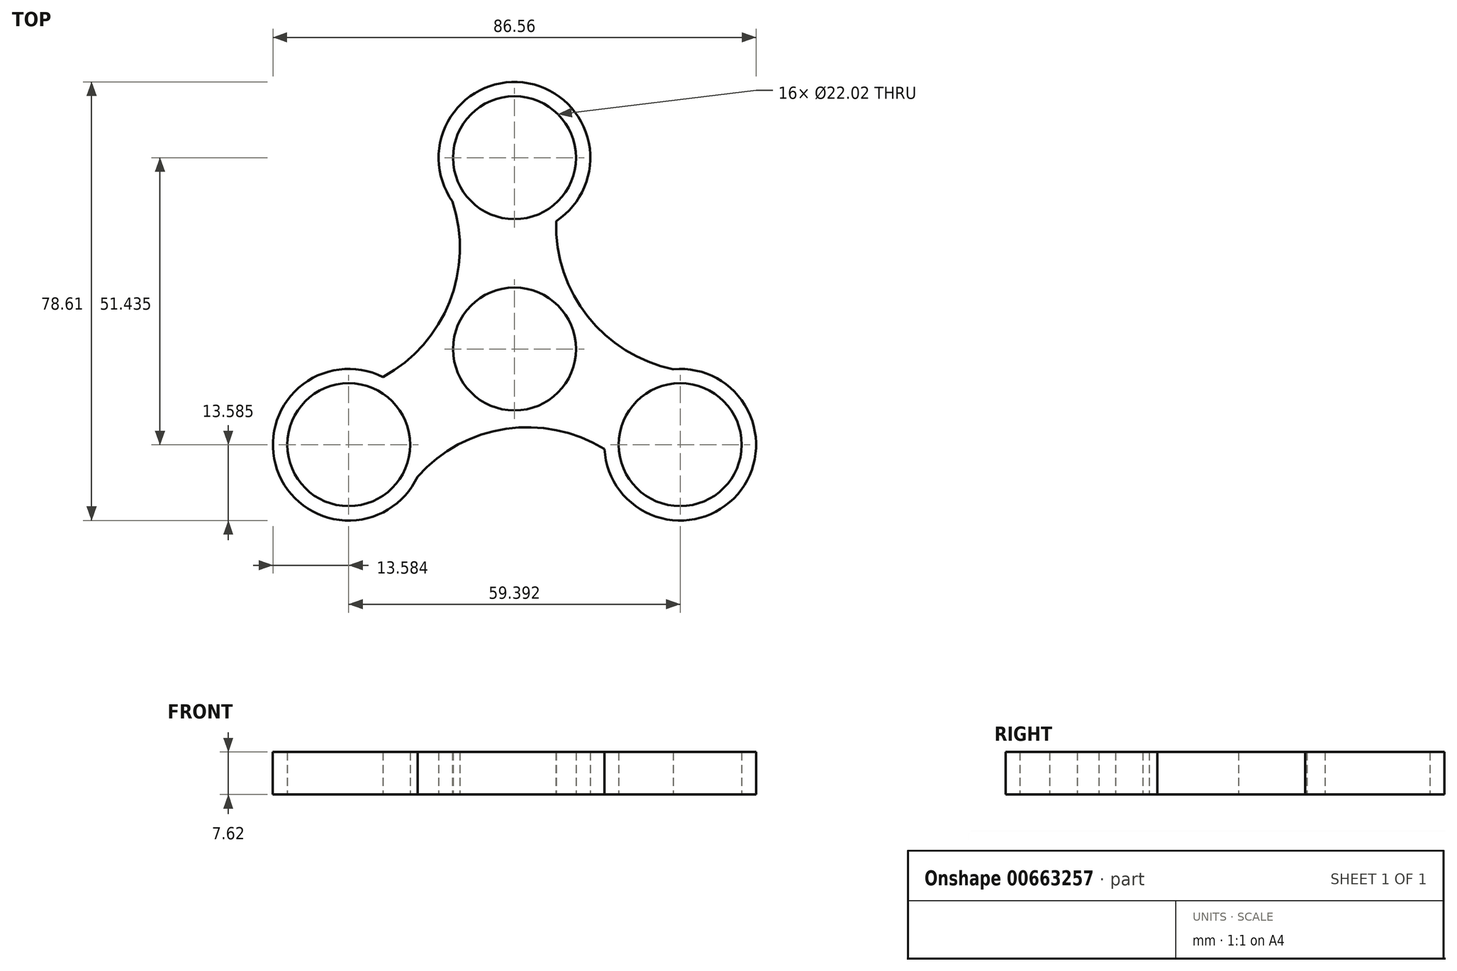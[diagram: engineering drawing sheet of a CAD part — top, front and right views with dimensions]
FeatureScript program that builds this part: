
annotation { "Feature Type Name" : "Feature", "Feature Type Description" : "" }
export const myFeature = defineFeature(function(context is Context, id is Id, definition is map)
    precondition{}
    {
        {
            var Q0;
            Q0=qCreatedBy(makeId("Top.planeOp"),FACE);
            var sketch = newSketch(context, id + "F0", { "sketchPlane" : qUnion([Q0])});
            skCircle(sketch, "E0", {"center": v(0, 0) * mm, "radius": 11.01 * mm});
            skCircle(sketch, "E1", {"center": v(0, 34.3) * mm, "radius": 11.01 * mm});
            skPoint(sketch, "E2.orphan", {"position": v(9.2, 28.24) * mm});
            skPoint(sketch, "E3.orphan", {"position": v(-9.2, 28.24) * mm});
            skPoint(sketch, "E4.end.orphan", {"position": v(12.28, 10.92) * mm});
            skPoint(sketch, "E5.start.orphan", {"position": v(-12.28, 10.92) * mm});
            skPoint(sketch, "E6.orphan", {"position": v(13.1, -18.76) * mm});
            skPoint(sketch, "E7.orphan", {"position": v(-18.8, -18.27) * mm});
            skCircle(sketch, "E8.1.0", {"center": v(-29.7, -17.14) * mm, "radius": 11.01 * mm});
            skCircle(sketch, "E8.2.0", {"center": v(29.7, -17.15) * mm, "radius": 11.01 * mm});
            skCircle(sketch, "E9", {"center": v(0, 34.3) * mm, "radius": 13.59 * mm});
            skCircle(sketch, "E10.1.0", {"center": v(-29.7, -17.14) * mm, "radius": 13.59 * mm});
            skCircle(sketch, "E10.2.0", {"center": v(29.7, -17.15) * mm, "radius": 13.59 * mm});
            skArc(sketch, "E11", {"start": v(-23.59, -5) * mm, "mid": v(-11.63, 8.46) * mm, "end": v(-11.1, 26.46) * mm});
            skArc(sketch, "E12.1.0", {"start": v(16.13, -17.92) * mm, "mid": v(-1.51, -14.3) * mm, "end": v(-17.36, -22.85) * mm});
            skArc(sketch, "E12.2.0", {"start": v(7.46, 22.93) * mm, "mid": v(13.14, 5.84) * mm, "end": v(28.47, -3.61) * mm});
            skSolve(sketch);
        }
        {
            var Q0;
            Q0=makeQuery(id+"F0.imprint","IMPRINT",FACE,{"disambiguationData":[TD([[makeQuery(id+"F0.imprint","IMPRINT",EDGE,{"derivedFrom":sQuery(id+"F0.wireOp",EDGE,"E0")}),-1.0]])]});
            var Q1;
            Q1=makeQuery(id+"F0.imprint","IMPRINT",FACE,{"disambiguationData":[TD([[makeQuery(id+"F0.imprint","IMPRINT",EDGE,{"derivedFrom":sQuery(id+"F0.wireOp",EDGE,"E8.2.0")}),-1.0]])]});
            var Q2;
            Q2=makeQuery(id+"F0.imprint","IMPRINT",FACE,{"disambiguationData":[TD([[makeQuery(id+"F0.imprint","IMPRINT",EDGE,{"derivedFrom":sQuery(id+"F0.wireOp",EDGE,"E8.1.0")}),-1.0]])]});
            var Q3;
            Q3=makeQuery(id+"F0.imprint","IMPRINT",FACE,{"disambiguationData":[TD([[makeQuery(id+"F0.imprint","IMPRINT",EDGE,{"derivedFrom":sQuery(id+"F0.wireOp",EDGE,"E1")}),-1.0]])]});
            extrude(context, id + "F1", {"entities" : qUnion([Q0, Q1, Q2, Q3]), "depth" : 7.62 * mm, "offsetDistance" : 25.4 * mm});
        }
    });
